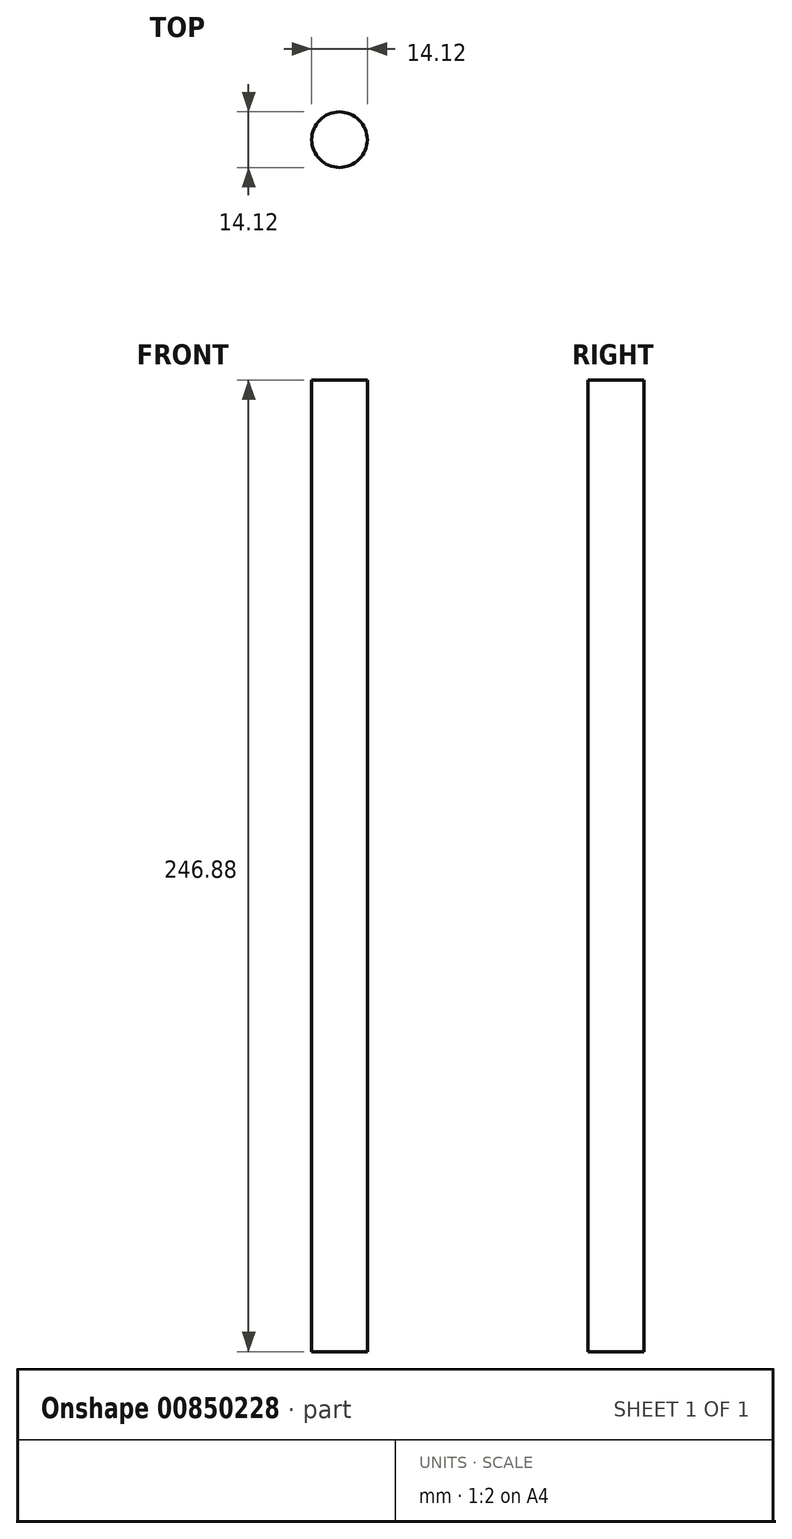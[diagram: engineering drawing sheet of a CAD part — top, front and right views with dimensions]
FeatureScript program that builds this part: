
annotation { "Feature Type Name" : "Feature", "Feature Type Description" : "" }
export const myFeature = defineFeature(function(context is Context, id is Id, definition is map)
    precondition{}
    {
        {
            var Q0;
            Q0=qCreatedBy(makeId("Top.planeOp"),FACE);
            var sketch = newSketch(context, id + "F0", { "sketchPlane" : qUnion([Q0])});
            skCircle(sketch, "E0", {"center": v(0, 0) * mm, "radius": 7.06 * mm});
            skSolve(sketch);
        }
        {
            var Q0;
            Q0=sQuery(id+"F0.wireOp",EDGE,"E0");
            extrude(context, id + "F1", {"bodyType" : ToolBodyType.SURFACE, "surfaceEntities" : qUnion([Q0]), "depth" : 246.88 * mm, "offsetDistance" : 25.4 * mm});
        }
    });
